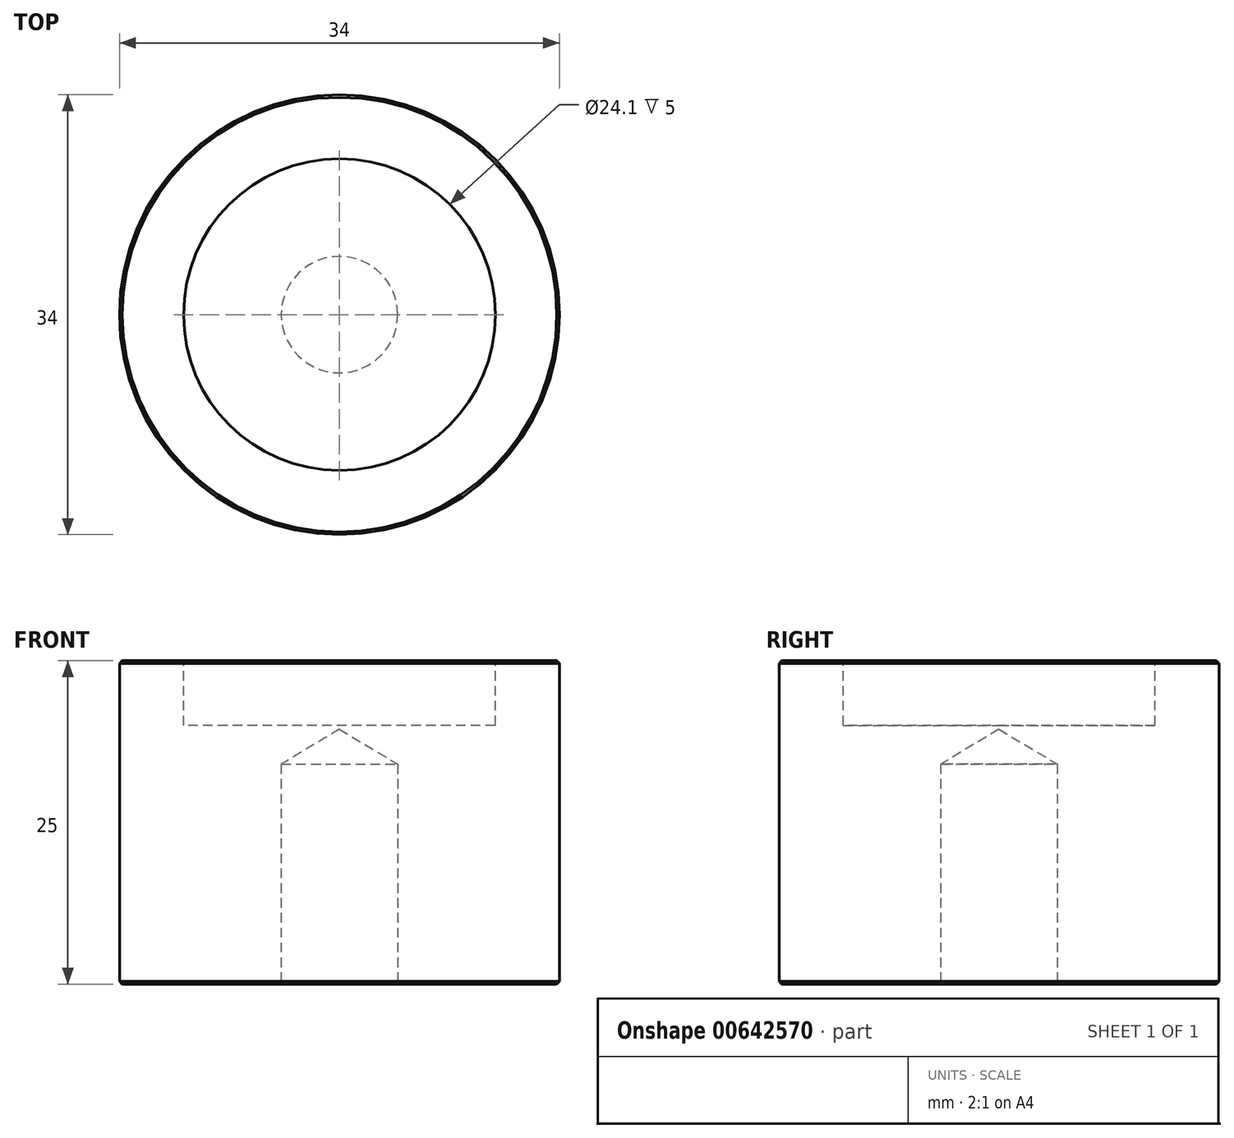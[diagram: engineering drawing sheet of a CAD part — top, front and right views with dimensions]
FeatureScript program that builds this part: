
annotation { "Feature Type Name" : "Feature", "Feature Type Description" : "" }
export const myFeature = defineFeature(function(context is Context, id is Id, definition is map)
    precondition{}
    {
        {
            var Q0;
            Q0=qCreatedBy(makeId("Top.planeOp"),FACE);
            var sketch = newSketch(context, id + "F0", { "sketchPlane" : qUnion([Q0])});
            skCircle(sketch, "E0", {"center": v(0, 0) * mm, "radius": 17 * mm});
            skSolve(sketch);
        }
        {
            var Q0;
            Q0 = qSketchRegion(id + "F0", true);
            extrude(context, id + "F1", {"entities" : qUnion([Q0]), "depth" : 25 * mm, "offsetDistance" : 25 * mm});
        }
        {
            var Q0;
            Q0=makeQuery(id+"F1.opExtrude","CAP_FACE",FACE,{"disambiguationData":[OSD([sQuery(id+"F0.wireOp",EDGE,"E0")])],"isStart":true});
            var sketch = newSketch(context, id + "F2", { "sketchPlane" : qUnion([Q0])});
            skPoint(sketch, "E1", {"position": v(0, 0) * mm});
            skSolve(sketch);
        }
        {
            var Q0;
            Q0=sQuery(id+"F2.wireOp",VERTEX,"E1");
            var Q1;
            Q1=makeQuery(id+"F1.opExtrude","SWEPT_BODY",BODY,{"disambiguationData":[OSD([sQuery(id+"F0.wireOp",EDGE,"E0")])]});
            hole(context, id + "F3", {"style" : HoleStyle.SIMPLE, "endStyle" : HoleEndStyle.BLIND, "standardTappedOrClearance" : lookupTablePath({ "standard" : "ISO", "size" : "9", "type" : "Drilled" }), "standardBlindInLast" : lookupTablePath({ "standard" : "ISO", "size" : "9", "type" : "Drilled" }), "holeDiameter" : 9 * mm, "majorDiameter" : 3 * mm, "holeDepth" : 17 * mm, "isTappedThrough" : true, "tappedDepth" : 5 * mm, "tapClearance" : 2, "startFromSketch" : true, "locations" : qUnion([Q0]), "scope" : qUnion([Q1])});
        }
        {
            var Q0;
            Q0=makeQuery(id+"F1.opExtrude","CAP_FACE",FACE,{"disambiguationData":[OSD([sQuery(id+"F0.wireOp",EDGE,"E0")])],"isStart":false});
            var sketch = newSketch(context, id + "F4", { "sketchPlane" : qUnion([Q0])});
            skCircle(sketch, "E2", {"center": v(0, 0) * mm, "radius": 12.05 * mm});
            skSolve(sketch);
        }
        {
            var Q0;
            Q0=makeQuery(id+"F4.imprint","IMPRINT",FACE,{"disambiguationData":[TD([[makeQuery(id+"F4.imprint","IMPRINT",EDGE,{"derivedFrom":sQuery(id+"F4.wireOp",EDGE,"E2")}),1.0]])]});
            extrude(context, id + "F5", {"entities" : qUnion([Q0]), "operationType" : NewBodyOperationType.REMOVE, "oppositeDirection" : true, "depth" : 5 * mm, "offsetDistance" : 25 * mm});
        }
        {
            var Q0;
            Q0=makeQuery(id+"F1.opExtrude","CAP_EDGE",EDGE,{"disambiguationData":[OSD([sQuery(id+"F0.wireOp",EDGE,"E0")])],"isStart":false});
            var Q1;
            Q1=makeQuery(id+"F5.boolean.opBoolean","COPY",EDGE,{"derivedFrom":makeQuery(id+"F5.opExtrude","CAP_EDGE",EDGE,{"disambiguationData":[OSD([sQuery(id+"F4.wireOp",EDGE,"E2")])],"isStart":true})});
            var Q2;
            Q2=makeQuery(id+"F1.opExtrude","CAP_EDGE",EDGE,{"disambiguationData":[OSD([sQuery(id+"F0.wireOp",EDGE,"E0")])],"isStart":true});
            var Q3;
            Q3=makeQuery(id+"F3.hole-0.boolean.opBoolean","COPY",EDGE,{"derivedFrom":makeQuery(id+"F3.hole-0.opRevolve","SWEPT_EDGE",EDGE,{"disambiguationData":[OSD([sQuery(id+"F3.hole-0.sketch.wireOp",EDGE,"core_line_2"),sQuery(id+"F3.hole-0.sketch.wireOp",EDGE,"core_line_3")])]})});
            chamfer(context, id + "F6", {"entities" : qUnion([Q0, Q1, Q2, Q3]), "width" : .2 * mm, "tangentPropagation" : true});
        }
    });
